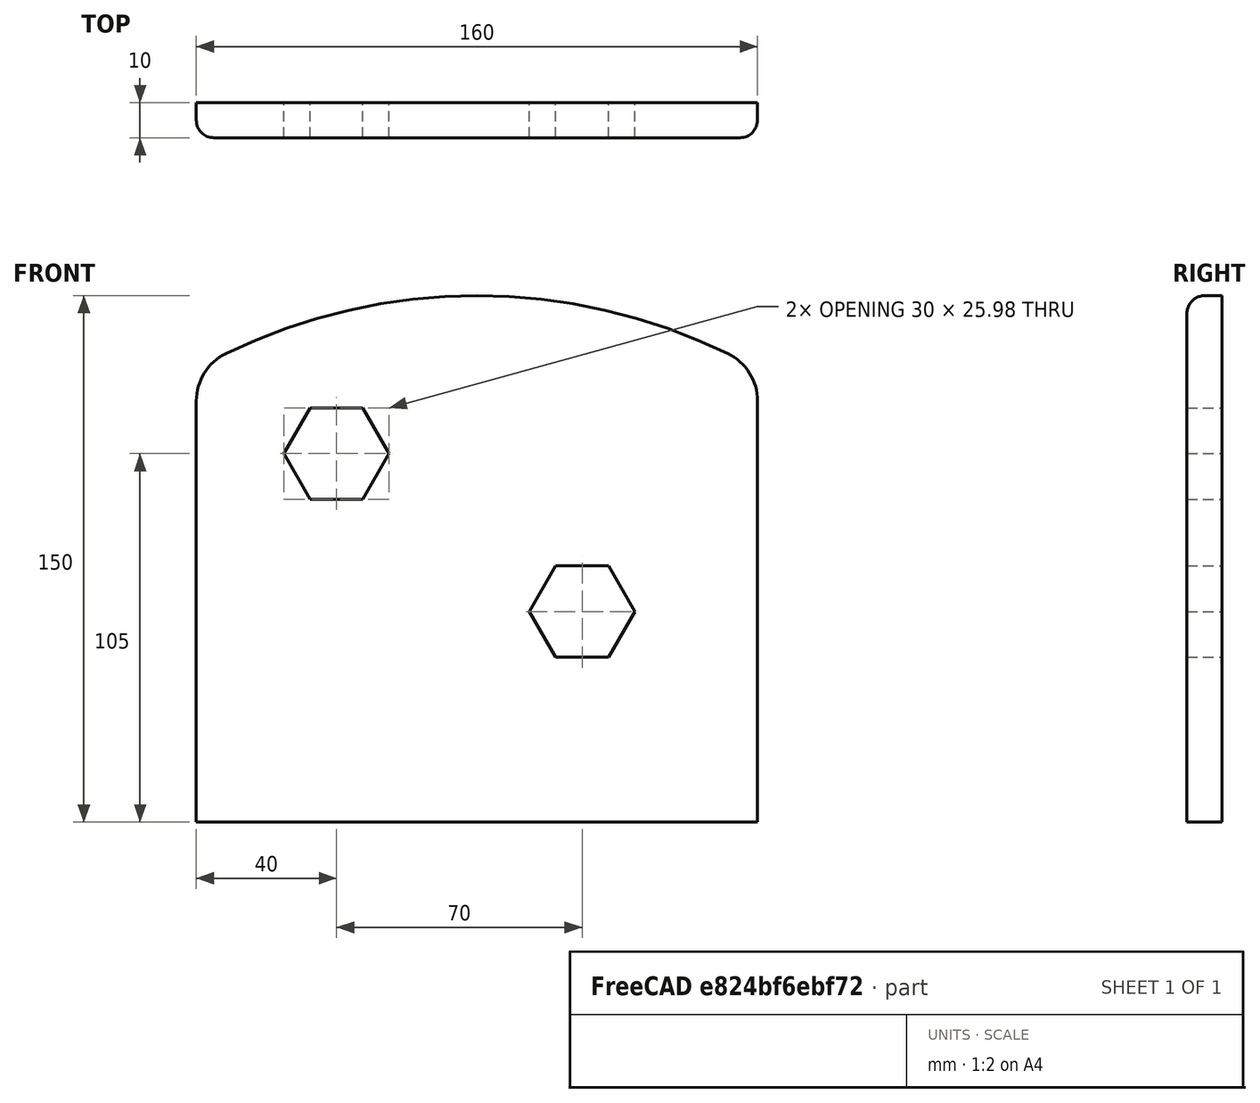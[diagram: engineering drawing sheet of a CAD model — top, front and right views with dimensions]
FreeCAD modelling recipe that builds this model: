
FCSTD DOCUMENT  (FreeCAD 0.19R)
Label: front_panel
License: CreativeCommons Attribution-ShareAlike
LicenseURL: http://creativecommons.org/licenses/by-sa/4.0/
objects: PartDesign::SubShapeBinder×3, PartDesign::Pocket×2, PartDesign::Pad×1, PartDesign::Fillet×1, PartDesign::Body×1, Part::Feature×1, App::Part×1
note: 12 computed .brp shape members not serialized (recipe doc carries the construction recipe); baked Part::Feature solids carry a one-line shape summary decoded from their .brp
EXTERNAL_REF file=base_dimensions.FCStd obj=Part
EXTERNAL_REF file=base_dimensions.FCStd obj=Sketch001
EXTERNAL_REF file=base_dimensions.FCStd obj=Sketch004

FEATURE [PartDesign::SubShapeBinder] Binder
  BindMode = 0
  ClaimChildren = false
  Context = -> Part [Body.Binder.]
  Fuse = false
  MakeFace = true
  PartialLoad = false
  Relative = true
  Support = -> [<external base_dimensions.FCStd>#Part[Body.Sketch.]]
  _Version = 1
FEATURE [PartDesign::Pad] Pad
  Length = 10
  Length2 = 100
  Profile = -> Binder [Face1]
  Type = 0
  expr: Length = <<base_dimensions>>#<<front_y>>.Constraints.thickness
FEATURE [PartDesign::SubShapeBinder] Binder001
  BindMode = 0
  ClaimChildren = false
  Context = -> Part [Body.Binder001.]
  Fuse = false
  MakeFace = true
  PartialLoad = false
  Relative = true
  Support = -> [<external base_dimensions.FCStd>#Part[Body001.Sketch002.]]
  _Version = 1
  expr: .Placement.Base.x = <<base_dimensions>>#<<box_positions>>.Constraints.p1_x
  expr: .Placement.Base.z = <<base_dimensions>>#<<box_positions>>.Constraints.p1_z
FEATURE [PartDesign::Pocket] Pocket
  BaseFeature = -> Pad
  Length = 5
  Length2 = 100
  Profile = -> Binder001 [Face1]
  Reversed = true
  Type = 1
FEATURE [PartDesign::SubShapeBinder] Binder002
  BindMode = 0
  ClaimChildren = false
  Context = -> Part [Body.Binder002.]
  Fuse = false
  MakeFace = true
  PartialLoad = false
  Relative = true
  Support = -> [<external base_dimensions.FCStd>#Part[Body001.Sketch002.]]
  _Version = 1
  expr: .Placement.Base.z = <<base_dimensions>>#<<box_positions>>.Constraints.p2_z
  expr: .Placement.Base.x = <<base_dimensions>>#<<box_positions>>.Constraints.p2_x
FEATURE [PartDesign::Pocket] Pocket001
  BaseFeature = -> Pocket
  Length = 5
  Length2 = 100
  Profile = -> Binder002 [Face1]
  Reversed = true
  Type = 1
FEATURE [PartDesign::Fillet] Fillet
  Base = -> Pocket001 [Edge11,Edge13,Edge12,Edge6,Edge3]
  BaseFeature = -> Pocket001
  Radius = 5
FEATURE [PartDesign::Body] Body  label="front_panel_body"
  Group = -> [Binder,Pad,Binder001,Pocket,Binder002,Pocket001,Fillet]
  Origin = -> Origin001
  Tip = -> Fillet
FEATURE [Part::Feature] Body__sc_export  label="front_panel_body__sc_export"
  shape: bbox 162.5 x 10 x 153.8 mm, 25 faces (baked)
FEATURE [App::Part] Part  label="front_panel_part"
  Group = -> [Body,Body__sc_export]
  Origin = -> Origin
